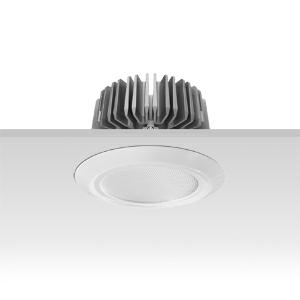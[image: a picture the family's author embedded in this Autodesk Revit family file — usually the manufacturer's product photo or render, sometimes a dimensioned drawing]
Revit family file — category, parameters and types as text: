
# Revit family: 3f_filippi_-_3f_reno_bianco_ampio_3f_filippi_-_30341_a01046_-_3f_reno_150_wh_2000-840_wide___smp_wh_9b5e
name_source: partatom
category: Lighting Fixtures
units: mm (PartAtom-declared; Revit-internal decimal feet)

## family parameters
Cut with Voids When Loaded = No
Host = Face
Light Source = No
Part Type = Normal
Room Calculation Point = No
Round Connector Dimension = Use Diameter
Shared = No

## types (1)
- 3F Filippi - 3F Reno Bianco Ampio (1 x LED, 1726 lm, 20 W, 4000 K)
    Apparent Load = 20 VA
    Approval mark = CE
    CIE Flux Codes = 73 92 98 100 100
    Color Rendering = 80
    Color Temperature = 4000 K
    Control Gear = Electronic ballast
    Default Elevation = 1800 mm
    Description = ILLUMINOTECHNICAL
Luminous efficiency 100% (DLOR 100%, ULOR 0%).
Initial luminous flux of the luminaire 1726 lm.
Direct symmetric wide distribution.
Installation Interdistance Transv.D = 1.01 x hu - Long.D = 1.00 x hu.
Tabular UGR (CIE 117 - 4H-8H; S=0.25H; 70/50/20): RUG 23.4 - 23.4.
Beam angle: 70° - 70°.
Luminous efficacy 86 lm/W.
Lifetime (L90/B10): 30000 h. (tq+25°C)
Lifetime (L85/B10): 50000 h. (tq+25°C)
Lifetime (L70/B10): 80000 h. (tq+25°C)
Sudden decreased luminous flux after 50000 hours: 0% (C0).
Photobiological safety in compliance with IEC/TR 62778: RG0 risk exempt, (IEC 62471).
In compliance with IEC/EN 62722-2-1 - IEC/EN 62717 standards.

SOURCE
Compact LED module 2000/840.
Energy efficiency class (UE 2019/2020 - UE 2019/2015): D.
CIE 13.3 Colour rendering index: CRI >80 (R9 <50%).
IES TM-30 Fidelity Index: Rf = 84 Rg = 95.
CCT nominal colour temperature 4000 K.
Colour initial tolerance (MacAdam): SDCM 3.
Zhaga Book 3 compliant.

MECHANICAL
Passive heat dissipator in die-casting aluminium, oversized, for optimum thermal management of the LED module.
Parabolic element with graduated/concentric rings in white polycarbonate.
Transparent external lens with glossy and satin differentiated surfaces, with a cooling and anti-insect system in methacrylate (PMMA).
Fastening spring clips in stainless steel.
Dimensions: diameter 176 mm, height 111 mm. Weight 0.74 kg.
IP44 protection degree for exposed part, IP20 for recessed part.
Mechanical strength to impacts IK05 (0.7 joule).
Glow-wire test resistance 650°C.

ELECTRICAL
Wiring on a separate unit.
Halogen Free electronic wiring 230V-50/60Hz, power factor 0.95, THD <25%, constant output current, SELV, class II, 1 driver.
Power of the luminaire 20 W.
ENEC - CE.
SAFE FLICKER: PstLM=<1 and SVM=<0.4 (IEC TR 61547-1 and IEC TR 63158), to ensure a more comfortable and safe light.
Luminaire compliant with EN 60598-2-22 for power supply from a centralised emergency system CPSS (Central Power Supply System), not incorporated in the luminaire - high risk areas excluded. The default power and flux are 100% in AC and 100% in DC.
Ambient temperature from 0°C to +25°C.
Temperature class T6 max 85°C.
Relative humidity UR: <85%.

INSTALLATION
Pull-up recessed fitting.
False ceiling carving: 150 mm.
All accessories dedicated to this product are available on the Catalog and on our website www.3F-Filippi.com.

ACCESSORIES
A01046 - Anti-glare microprismatic SMP diffuser in methacrylate (PMMA), locked and in line with the trim, in white polycarbonate.

APPLICATIONS
Suitable product for food production plants (HACCP), IFS (Food Version 6), BRC (GSFS Food Version 7).
Environments: architectural, commercial, exhibition areas, transit areas, corridors, shops, display windows, service areas.
In false ceilings with narrow voids.

WARNING
Luminaire designed for disposal/recycling at end-of-life.
Replaceable (LED only) light source by a professional. Replaceable control gear by a professional.
    Height = 0 mm  [stored 0 ft]
    Lamp = 1 x LED
    Lamp Light Flux = 1726 lm
    Lamp Power = 20 W
    Lamp count = 1
    Length = 176 mm
    Lifetime = 50000 h
    Luminous efficacy = 86 lm/W
    Manufacturer = 3F Filippi
    ModVariant = No
    Model = 3F Filippi - 30341+A01046 - 3F Reno 150 WH 2000-840 WIDE + SMP WH
    Mounting Place = Ceiling
    Mounting Type = Recessed
    Number of Poles = 1
    OnlyDefault = Yes
    Power Factor = 1
    Product Name = 3F Filippi - 3F Reno Bianco Ampio
    Product group = recessed luminaire
    ProductGroupID = 4
    Protection Class = Protection class II
    Protection Degree = IP 20
    RLX_Detail_Level = 1
    RLX_Emergency_Light_Flux = 0 lm
    RLX_Emergency_Type = 0
    RLX_Emergency_Type_DB = No
    RlxData = <blob elided: 84201 chars, md5=88c3b580>
    Socket = socket
    Standby Power = 0 W
    System Light Flux = 1726 lm
    System Power = 20 W
    Type Comments = Product without accessories
    Type Image = 3ffilippi_3f_reno_150_wh_vs_smp.jpg
    URL = http://relux.com
    VarID = ---
    Voltage = 0 V
    Weight = 0.00 kg
    Width = 0 mm  [stored 0 ft]

note: [stored X ft] marks values corroborated as IEEE doubles in the binary element streams (Revit-internal decimal feet)

## geometry (parser evidence)
native form markers: Blend x4, Sweep x9
no freeform markers — native parametric forms only
